AUTODESK INVENTOR PART (.ipt)
format: ipt  version: 2014 (Build 180170000, 170)  size: 86,016 bytes
history: native  units: in
note: dims shown in document units (in); Inventor stores cm internally (conversion verified against a paired STEP export)
features: sketch x1
ambient origin geometry x8: Origin, YZ Plane, XZ Plane, XY Plane, X Axis, Y Axis, Z Axis, Center Point
feature tree (1):
  sketch  "Sketch1"  dims[d0=24.0in d1=15.875in d2=3.703in d3=7.26in d4=8.533in d5=1.5in d6=1.5in d7=25.0in d8=7.243in d9=15.875in d10=7.26in d11=10.533in d12=15.875in d13=7.26in d14=8.033in d15=13.4967in d16=25.0in d17=22.0in d18=1.23in d19=8.6073in]
